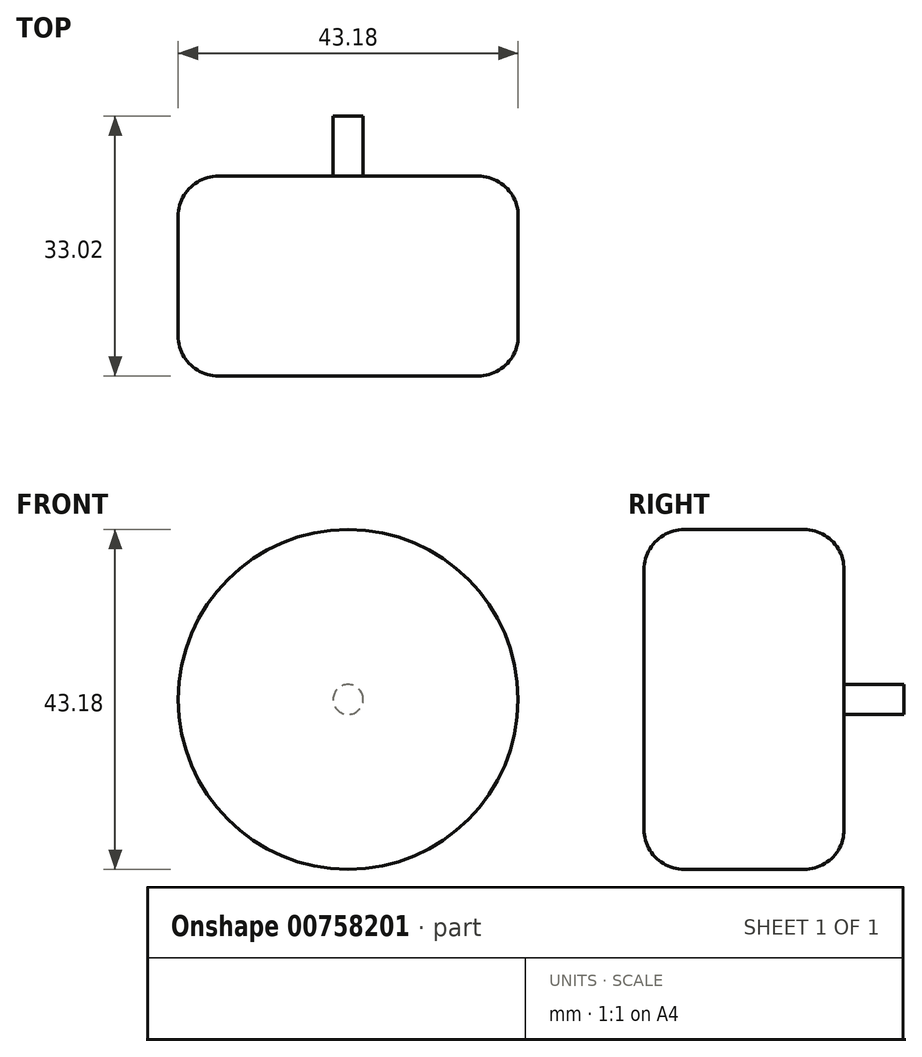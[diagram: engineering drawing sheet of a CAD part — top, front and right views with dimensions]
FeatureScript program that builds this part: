
annotation { "Feature Type Name" : "Feature", "Feature Type Description" : "" }
export const myFeature = defineFeature(function(context is Context, id is Id, definition is map)
    precondition{}
    {
        {
            var Q0;
            Q0=qCreatedBy(makeId("Front.planeOp"),FACE);
            var sketch = newSketch(context, id + "F0", { "sketchPlane" : qUnion([Q0])});
            skCircle(sketch, "E0", {"center": v(0, 0) * mm, "radius": 1.9 * mm});
            skSolve(sketch);
        }
        {
            var Q0;
            Q0 = qSketchRegion(id + "F0", true);
            extrude(context, id + "F1", {"entities" : qUnion([Q0]), "depth" : 7.62 * mm, "offsetDistance" : 25.4 * mm});
        }
        {
            var Q0;
            Q0=makeQuery(id+"F1.opExtrude","CAP_FACE",FACE,{"disambiguationData":[OSD([sQuery(id+"F0.wireOp",EDGE,"E0")])],"isStart":false});
            var sketch = newSketch(context, id + "F2", { "sketchPlane" : qUnion([Q0])});
            skCircle(sketch, "E1", {"center": v(0, 0) * mm, "radius": 21.59 * mm});
            skSolve(sketch);
        }
        {
            var Q0;
            Q0 = qSketchRegion(id + "F2", true);
            extrude(context, id + "F3", {"entities" : qUnion([Q0]), "operationType" : NewBodyOperationType.ADD, "depth" : 25.4 * mm, "offsetDistance" : 25.4 * mm});
        }
        {
            var Q0;
            Q0=makeQuery(id+"F3.opExtrude","CAP_EDGE",EDGE,{"disambiguationData":[OSD([sQuery(id+"F2.wireOp",EDGE,"E1")])],"isStart":false});
            var Q1;
            Q1=makeQuery(id+"F3.opExtrude","CAP_EDGE",EDGE,{"disambiguationData":[OSD([sQuery(id+"F2.wireOp",EDGE,"E1")])],"isStart":true});
            fillet(context, id + "F4", {"entities" : qUnion([Q0, Q1]), "radius" : 5.08 * mm, "tangentPropagation" : true, "allowEdgeOverflow" : false});
        }
    });
